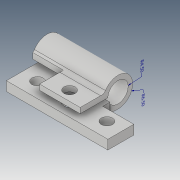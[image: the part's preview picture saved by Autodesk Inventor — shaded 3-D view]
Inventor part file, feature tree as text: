
AUTODESK INVENTOR PART (.ipt)
format: ipt  version: 2019 (Build 230136000, 136)  size: 488,960 bytes
history: native  units: mm
features: extrude x26, sketch x24, other x10, plane x9, projected_geometry x9, direct_edit x5, move_body x4, fillet x3, reference x3, split x2, boolean_combine x1
ambient origin geometry x8: Origin, YZ Plane, XZ Plane, XY Plane, X Axis, Y Axis, Z Axis, Center Point
bodies: Solid1 (feature_tree), Solid2 (feature_tree), Solid3 (feature_tree), Solid4 (feature_tree), Solid5 (feature_tree)
feature tree (96):
  other  "Annotations"
  extrude  "Extrusion1"  Depth=45.0mm
  extrude  "Extrusion4"  Depth=5.0mm
  fillet  "Fillet1"  Radius=11.0mm
  extrude  "Extrusion5"  Depth=23.0mm
  plane  "Work Plane1"
  extrude  "Extrusion6"  Depth=10.0mm
  direct_edit  "Direct Edit1"
  extrude  "Extrusion7"  Depth=12.0mm
  fillet  "Fillet2"  Radius=5.0mm
  plane  "Work Plane5"
  extrude  "Extrusion8"  Depth=3.0mm
  plane  "Work Plane6"
  extrude  "Extrusion9"  Depth=17.8mm
  sketch  "Sketch12"  dims[d34=5.0mm d35=17.8mm]
  extrude  "Extrusion12"  Depth=17.8mm
  extrude  "Extrusion13"  Depth=30.8mm
  extrude  "Extrusion15"  Depth=3.0mm TaperAngle=0.0deg
  plane  "Work Plane7"
  extrude  "Extrusion16"  TaperAngle=0.0deg  [1 undecoded]
  extrude  "Extrusion17"  Depth=18.0mm
  plane  "Work Plane8"
  plane  "Work Plane9"
  split  "Split1"
  split  "Split2"
  boolean_combine  "Combine1"
  direct_edit  "Direct Edit2"
  extrude  "Extrusion18"  Depth=2.0mm
  extrude  "Extrusion20"  Depth=0.5mm TaperAngle=0.0deg
  extrude  "Extrusion21"  Depth=7.25mm TaperAngle=0.0deg
  extrude  "Extrusion22"  Depth=7.25mm TaperAngle=0.0deg
  extrude  "Extrusion23"  Depth=10.0mm TaperAngle=0.0deg
  extrude  "Extrusion24"  Depth=10.0mm
  direct_edit  "Direct Edit3"
  extrude  "Extrusion25"  [1 undecoded]
  sketch  "Sketch24"  dims[d80=10.0mm d81=0.0mm d82=15.0mm]
  plane  "Work Plane10"
  extrude  "Extrusion26"  Depth=3.15mm TaperAngle=0.0deg
  sketch  "Sketch25"  dims[d83=3.0mm d88=-6.0mm]
  plane  "Work Plane11"
  extrude  "Extrusion27"  TaperAngle=0.0deg  [1 undecoded]
  sketch  "Sketch26"  dims[d89=7.5mm d90=3.15mm d91=0.0mm]
  extrude  "Extrusion28"  TaperAngle=0.0deg  [1 undecoded]
  extrude  "Extrusion29"  TaperAngle=0.0deg  [1 undecoded]
  direct_edit  "Direct Edit4"
  sketch  "Sketch28"  dims[d95=0.0mm d96=0.0mm d97=0.0mm d98=-0.3mm]
  plane  "Work Plane12"
  extrude  "Extrusion30"  Depth=10.0mm TaperAngle=0.0deg
  direct_edit  "Direct Edit5"
  extrude  "Extrusion31"  Depth=4.5mm TaperAngle=0.0deg
  extrude  "Extrusion32"  Depth=4.5mm TaperAngle=0.0deg
  fillet  "Fillet3"  Radius=1.65mm
  sketch  "Sketch1"  dims[d0=6.0mm d1=0.0mm d4=45.0mm]
  sketch  "Sketch5"  dims[d5=5.0mm d6=5.0mm d7=11.0mm]
  sketch  "Sketch6"  dims[d8=11.0mm d9=23.0mm]
  sketch  "Sketch7"  dims[d10=10.0mm d20=13.0mm]
  sketch  "Sketch8"  dims[d24=3.0mm d25=0.0mm d26=12.0mm d27=5.0mm]
  sketch  "Sketch10"  dims[d28=3.0mm d29=0.0mm d33=5.0mm]
  projected_geometry  "Projected Loop2"
  sketch  "Sketch13"  dims[d36=8.0mm d37=17.8mm]
  sketch  "Sketch14"  dims[d38=7.1mm d39=30.8mm]
  sketch  "Sketch15"  dims[d40=7.1mm d41=3.0mm d42=0.0mm]
  sketch  "Sketch17"  dims[d46=0.0mm d47=0.0mm d48=-2.5mm d49=0.0mm d50=0.0mm d51=-2.5mm]
  sketch  "Sketch18"  dims[d52=18.0mm d53=11.0mm]
  sketch  "Sketch19"  dims[d54=2.0mm d55=0.0mm d56=2.0mm]
  projected_geometry  "Projected Loop5"
  sketch  "Sketch20"  dims[d57=0.0mm d58=0.5mm d59=0.0mm]
  projected_geometry  "Projected Loop6"
  sketch  "Sketch21"  dims[d60=0.0mm d61=7.25mm d62=0.0mm]
  projected_geometry  "Projected Loop7"
  sketch  "Sketch22"  dims[d68=5.0mm d69=7.25mm d70=0.0mm]
  projected_geometry  "Projected Loop8"
  sketch  "Sketch23"  dims[d72=2.0mm d73=10.0mm d74=0.0mm]
  reference  "Reference1"
  projected_geometry  "Projected Loop9"
  reference  "Reference3"
  reference  "Reference4"
  sketch  "Sketch27"  dims[d92=2.0mm d93=0.0mm d94=0.0mm]
  projected_geometry  "Projected Loop10"
  sketch  "Sketch29"  dims[d99=0.3mm d100=0.0mm]
  projected_geometry  "Projected Loop11"
  sketch  "Sketch30"  dims[d101=10.0mm d102=0.0mm d105=10.0mm d106=0.0mm d110=1.45mm d111=0.0mm d112=1.45mm d113=0.0mm d114=1.65mm d115=0.0mm d116=0.105mm d117=0.0mm d118=-0.105mm d119=0.105mm d120=0.0mm d121=0.105mm d122=0.0mm d123=0.105mm d124=0.0mm d125=0.0mm d126=0.0mm d127=0.105mm d128=0.0mm d129=-2.0mm d130=10.0mm d131=0.0mm d132=0.0mm d133=0.0mm d134=1.76mm d135=1.0mm d136=0.0mm d137=1.0mm d138=0.0mm d139=2.0mm d84=49.911908mm d85=6.5mm d86=52.109261mm d87=4.5mm]
  projected_geometry  "Projected Loop12"
  other  "Composite1"
  move_body  "Move1"
  move_body  "Move2"
  move_body  "Move3"
  other  "Size1"
  other  "Srf1"
  parser-record x1  (decoder bookkeeping rows leaked as tree rows — omitted from the tree; the rows remain in map.json)
  other  "Cerniera versione 3.iam"
  other  "Cerniera 5.5:1"
  other  "Size2"
  move_body  "Move4"
  other  "Radial Dimension 1"
  other  "Radial Dimension 2"
note: 5 required parameter values undecoded (feature->parameter linkage not recoverable at this tier; creation-order binding heuristic only, values carry confidence <= 0.55)
note: 1 file-system path scrubbed to <path> (originals preserved in map.json)
